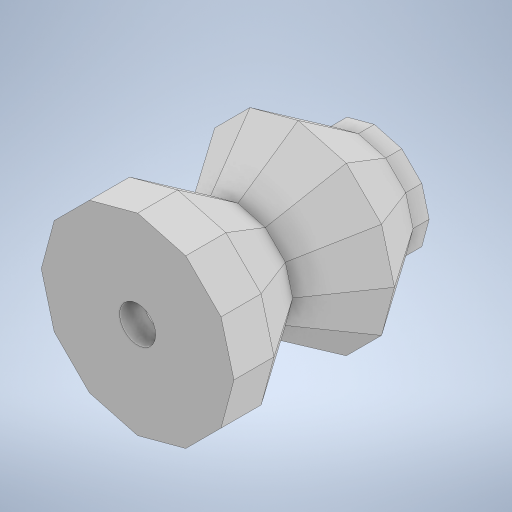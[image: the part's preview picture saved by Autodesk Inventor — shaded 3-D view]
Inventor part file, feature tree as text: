
AUTODESK INVENTOR PART (.ipt)
format: ipt  version: 2023 (Build 270158000, 158)  size: 355,328 bytes
history: native  units: in
note: dims shown in document units (in); Inventor stores cm internally (conversion verified against a paired STEP export)
features: sketch x7, extrude x5, projected_geometry x3, mirror x2, other x1, shell x1
ambient origin geometry x8: Origin, YZ Plane, XZ Plane, XY Plane, X Axis, Y Axis, Z Axis, Center Point
bodies: Body1 (feature_tree)
feature tree (19):
  other  "솔리드1"
  extrude  "돌출1"  Depth=0.9449in
  mirror  "미러1"
  mirror  "미러2"
  sketch  "스케치2"
  sketch  "스케치3"
  extrude  "돌출6"  Depth=0.2953in
  shell  "쉘2"  Thickness=0.0984in
  extrude  "돌출7"  Depth=0.0787in
  extrude  "돌출8"  Depth=0.0197in
  extrude  "돌출9"  Depth=0.0984in TaperAngle=0.0deg
  sketch  "스케치1"
  sketch  "스케치8"
  projected_geometry  "투영된 루프4"
  sketch  "스케치9"
  projected_geometry  "투영된 루프5"
  sketch  "스케치10"
  sketch  "스케치11"
  projected_geometry  "투영된 루프6"
